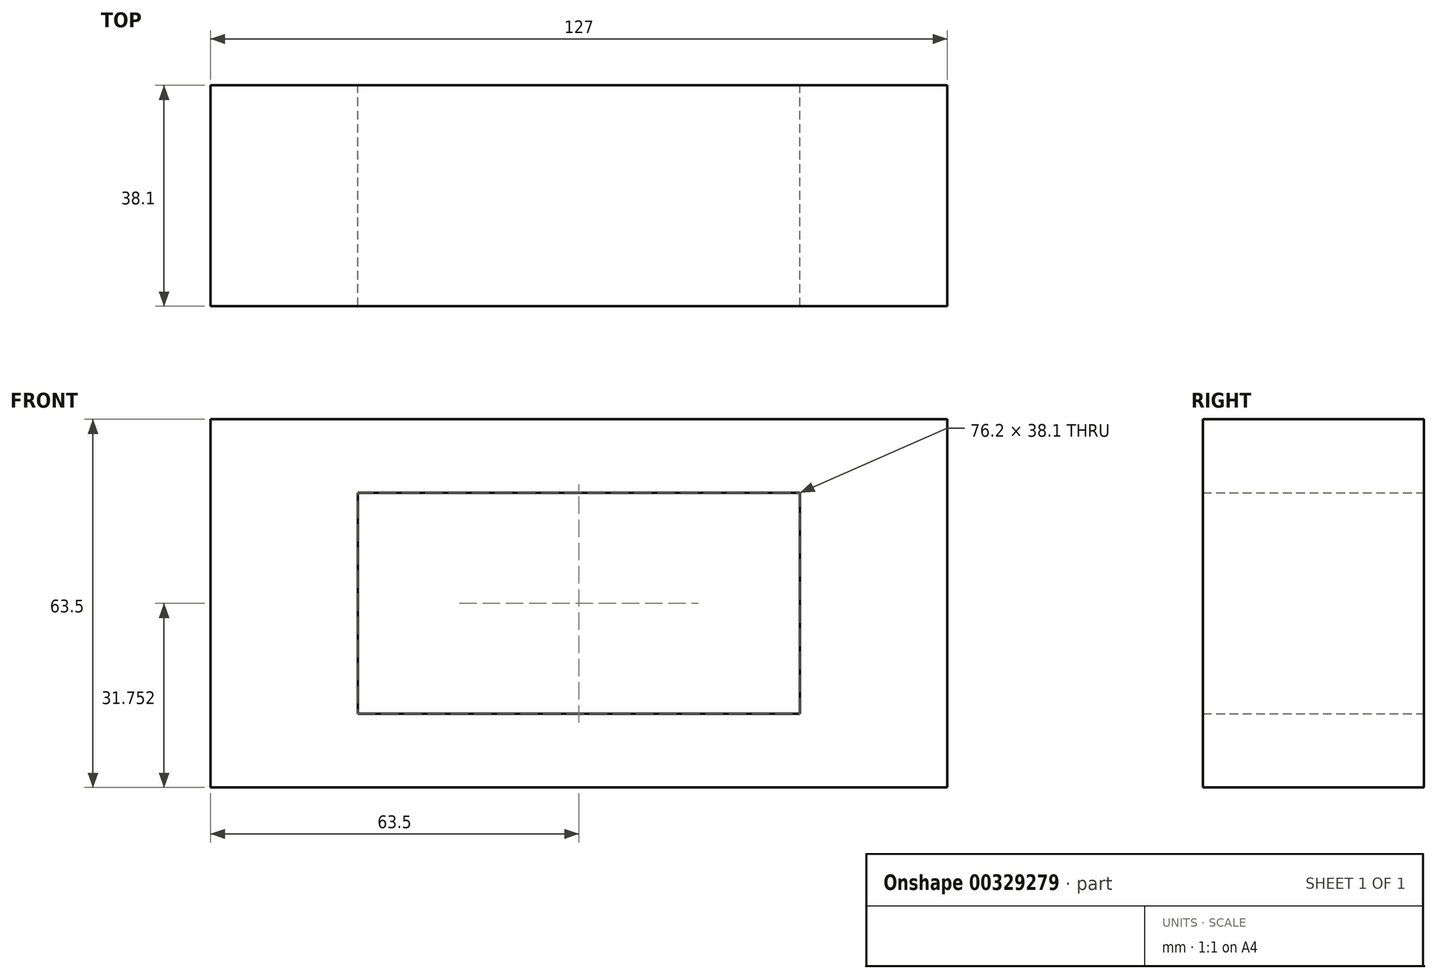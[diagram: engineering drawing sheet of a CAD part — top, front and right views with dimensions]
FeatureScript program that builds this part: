
annotation { "Feature Type Name" : "Feature", "Feature Type Description" : "" }
export const myFeature = defineFeature(function(context is Context, id is Id, definition is map)
    precondition{}
    {
        {
            var Q0;
            Q0=qCreatedBy(makeId("Front.planeOp"),FACE);
            var sketch = newSketch(context, id + "F0", { "sketchPlane" : qUnion([Q0])});
            skLineSegment(sketch, "E0", {"start": v(-56.58, 43.6) * mm, "end": v(70.42, 43.6) * mm});
            skLineSegment(sketch, "E1", {"start": v(-56.58, 43.6) * mm, "end": v(-56.58, -19.9) * mm});
            skLineSegment(sketch, "E2", {"start": v(70.42, 43.6) * mm, "end": v(70.42, -19.9) * mm});
            skLineSegment(sketch, "E3", {"start": v(70.42, -19.9) * mm, "end": v(-56.58, -19.9) * mm});
            skPoint(sketch, "E4", {"position": v(-56.58, 30.9) * mm});
            skPoint(sketch, "E5", {"position": v(-31.18, 30.9) * mm});
            skPoint(sketch, "E6", {"position": v(-56.58, -7.2) * mm});
            skPoint(sketch, "E7", {"position": v(-31.18, -7.2) * mm});
            skLineSegment(sketch, "E8", {"start": v(-31.18, 30.9) * mm, "end": v(-31.18, -7.2) * mm});
            skPoint(sketch, "E9", {"position": v(70.42, 30.9) * mm});
            skPoint(sketch, "E10", {"position": v(70.42, -7.2) * mm});
            skPoint(sketch, "E11", {"position": v(45.02, -7.2) * mm});
            skPoint(sketch, "E12", {"position": v(45.02, 30.9) * mm});
            skLineSegment(sketch, "E13", {"start": v(-31.18, 30.9) * mm, "end": v(45.02, 30.9) * mm});
            skLineSegment(sketch, "E14", {"start": v(45.02, -7.2) * mm, "end": v(45.02, 30.9) * mm});
            skLineSegment(sketch, "E15", {"start": v(-31.18, -7.2) * mm, "end": v(45.02, -7.2) * mm});
            skSolve(sketch);
        }
        {
            var Q0;
            Q0 = qSketchRegion(id + "F0", true);
            extrude(context, id + "F1", {"entities" : qUnion([Q0]), "depth" : 38.1 * mm});
        }
    });
